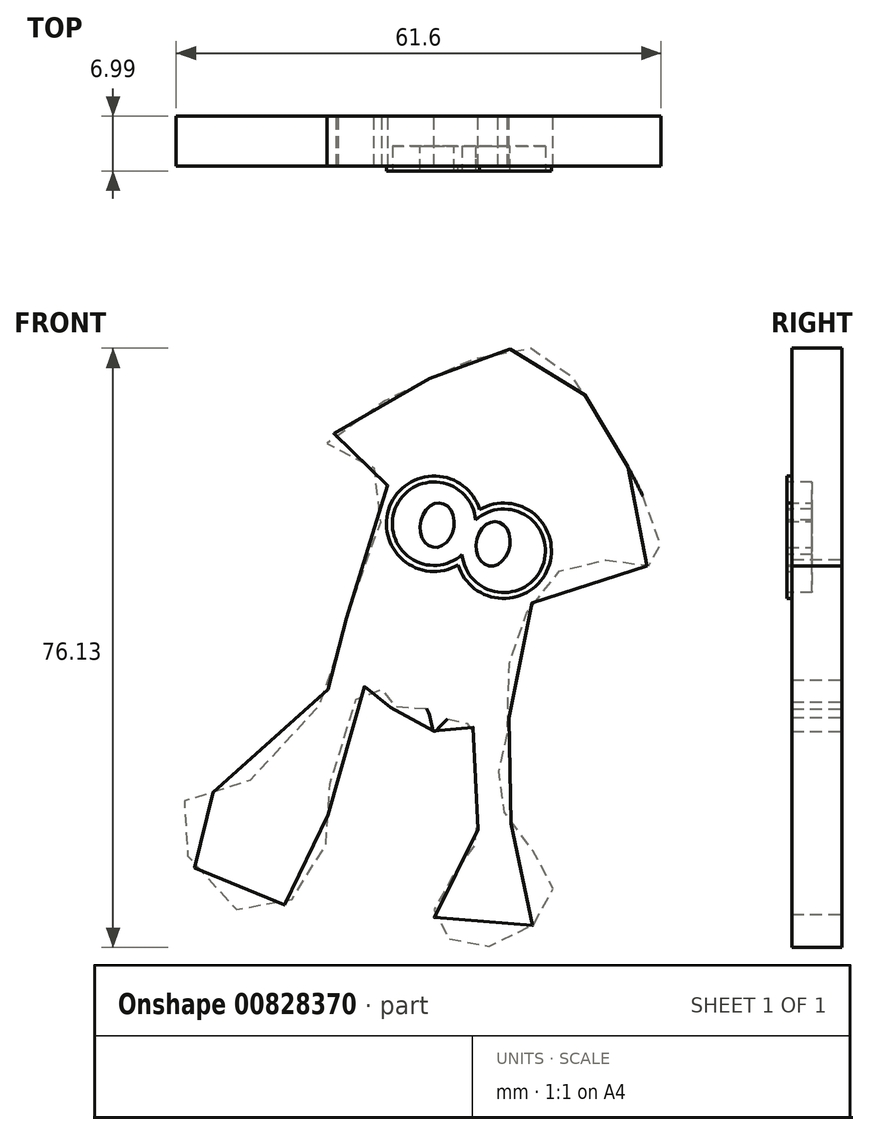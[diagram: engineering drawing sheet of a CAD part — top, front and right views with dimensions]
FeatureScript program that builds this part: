
annotation { "Feature Type Name" : "Feature", "Feature Type Description" : "" }
export const myFeature = defineFeature(function(context is Context, id is Id, definition is map)
    precondition{}
    {
        {
            var Q0;
            Q0=qCreatedBy(makeId("Front.planeOp"),FACE);
            var sketch = newSketch(context, id + "F0", { "sketchPlane" : qUnion([Q0])});
            skFitSpline(sketch, "E0", {"points": [v(24.63, 20.1) * mm, v(22.67, 23.28) * mm, v(18.26, 30.63) * mm, v(12.87, 35.04) * mm, v(5.12, 33.8) * mm, v(0, 31.61) * mm, v(-4.23, 29.54) * mm, v(-13.6, 22.79) * mm, v(-6.74, 19.36) * mm, v(-8.7, 8.33) * mm, v(-12.38, -3.48) * mm, v(-12.4, -3.59) * mm, v(-12.13, -4.17) * mm, v(-22.46, -19.18) * mm, v(-32.43, -23.05) * mm, v(-28.8, -33.08) * mm, v(-20.96, -36.51) * mm, v(-14.1, -29.16) * mm, v(-13.29, -20.6) * mm, v(-7.96, -7.04) * mm, v(-6.62, -7.78) * mm, v(-7.48, -10.54) * mm, v(-2.9, -9.73) * mm, v(-2.9, -9.73) * mm, v(-1.04, -10.5) * mm, v(0, -13.48) * mm, v(2.1, -11.74) * mm, v(4.36, -12.53) * mm, v(4.84, -12.67) * mm, v(5.2, -21.08) * mm, v(5, -28.19) * mm, v(0, -36.3) * mm, v(5.27, -40.92) * mm, v(15.1, -33.95) * mm, v(8.55, -22.93) * mm, v(9.43, -12.99) * mm, v(9.44, -5.64) * mm, v(18.26, 8.09) * mm, v(28.55, 8.09) * mm, v(24.63, 20.1) * mm]});
            skSolve(sketch);
        }
        {
            var Q0;
            Q0 = qSketchRegion(id + "F0", true);
            extrude(context, id + "F1", {"entities" : qUnion([Q0]), "depth" : 6.35 * mm, "offsetDistance" : 25.4 * mm});
        }
        {
            var Q0;
            Q0=makeQuery(id+"F1.opExtrude","CAP_FACE",FACE,{"disambiguationData":[OSD([sQuery(id+"F0.wireOp",EDGE,"E0")])],"isStart":false});
            var sketch = newSketch(context, id + "F2", { "sketchPlane" : qUnion([Q0])});
            skCircle(sketch, "E1", {"center": v(0, 12.9) * mm, "radius": 5.3 * mm});
            skCircle(sketch, "E2", {"center": v(8.84, 9.46) * mm, "radius": 5.3 * mm});
            skSolve(sketch);
        }
        {
            var Q0;
            Q0 = qSketchRegion(id + "F2", true);
            extrude(context, id + "F3", {"entities" : qUnion([Q0]), "operationType" : NewBodyOperationType.REMOVE, "oppositeDirection" : true, "depth" : 2.54 * mm, "offsetDistance" : 25.4 * mm});
        }
        {
            var Q0;
            Q0=makeQuery(id+"F3.boolean.opBoolean","COPY",FACE,{"derivedFrom":makeQuery(id+"F3.opExtrude","CAP_FACE",FACE,{"disambiguationData":[OSD([sQuery(id+"F2.wireOp",EDGE,"E1"),sQuery(id+"F2.wireOp",EDGE,"E2")])],"isStart":false})});
            var sketch = newSketch(context, id + "F4", { "sketchPlane" : qUnion([Q0])});
            skEllipse(sketch, "E3", {"center": v(7.49, 10.35) * mm, "majorRadius": 2.85 * mm, "minorRadius": 2.13 * mm, "majorAxis": v(-0.19, -0.98)});
            skEllipse(sketch, "E4", {"center": v(0.39, 12.72) * mm, "majorRadius": 2.85 * mm, "minorRadius": 2.13 * mm, "majorAxis": v(-0.19, -0.98)});
            skSolve(sketch);
        }
        {
            var Q0;
            Q0 = qSketchRegion(id + "F4", true);
            extrude(context, id + "F5", {"entities" : qUnion([Q0]), "operationType" : NewBodyOperationType.ADD, "depth" : 3.17 * mm, "offsetDistance" : 25.4 * mm});
        }
        {
            var Q0;
            Q0=makeQuery(id+"F1.opExtrude","CAP_FACE",FACE,{"disambiguationData":[OSD([sQuery(id+"F0.wireOp",EDGE,"E0")])],"isStart":false});
            var sketch = newSketch(context, id + "F6", { "sketchPlane" : qUnion([Q0])});
            skArc(sketch, "E5.0", {"start": v(3.05, 7.66) * mm, "mid": v(14.49, 7.26) * mm, "end": v(5.8, 14.7) * mm});
            skArc(sketch, "E5.1", {"start": v(5.8, 14.7) * mm, "mid": v(-5.65, 15.1) * mm, "end": v(3.05, 7.66) * mm});
            skArc(sketch, "E6.0", {"start": v(5.28, 13.39) * mm, "mid": v(-4.94, 14.83) * mm, "end": v(3.56, 8.97) * mm});
            skArc(sketch, "E6.1", {"start": v(3.56, 8.97) * mm, "mid": v(13.78, 7.53) * mm, "end": v(5.28, 13.39) * mm});
            skSolve(sketch);
        }
        {
            var Q0;
            Q0 = qSketchRegion(id + "F6", true);
            extrude(context, id + "F7", {"entities" : qUnion([Q0]), "operationType" : NewBodyOperationType.ADD, "depth" : 0.64 * mm, "offsetDistance" : 25.4 * mm});
        }
    });
